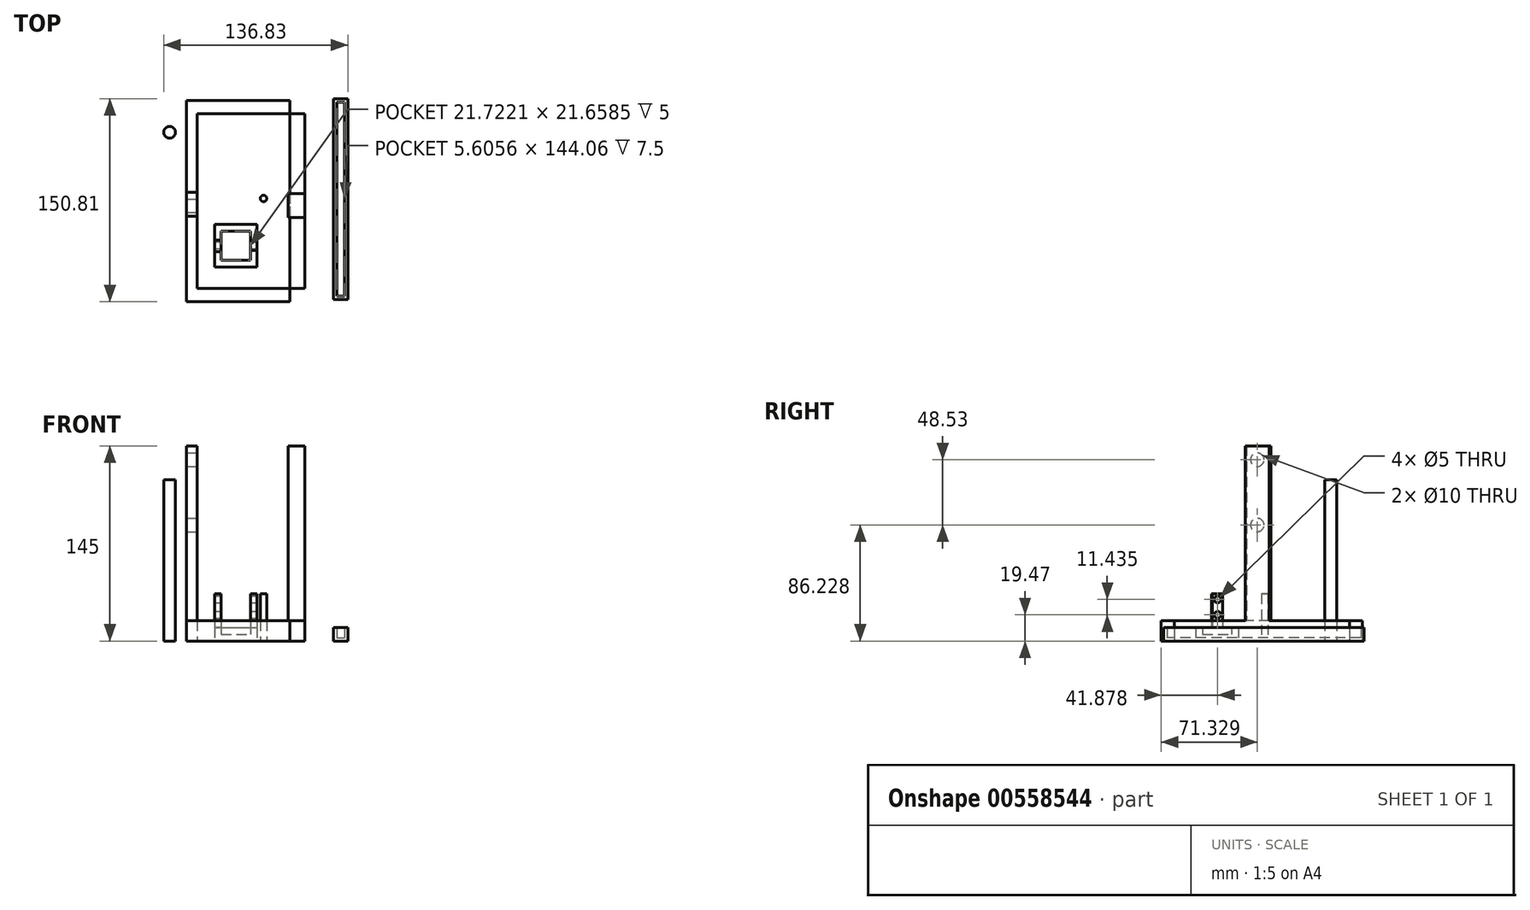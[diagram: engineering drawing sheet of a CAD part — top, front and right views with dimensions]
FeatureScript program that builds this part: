
annotation { "Feature Type Name" : "Feature", "Feature Type Description" : "" }
export const myFeature = defineFeature(function(context is Context, id is Id, definition is map)
    precondition{}
    {
        {
            var Q0;
            Q0=qCreatedBy(makeId("Top.planeOp"),FACE);
            var sketch = newSketch(context, id + "F0", { "sketchPlane" : qUnion([Q0])});
            skLineSegment(sketch, "E0.bottom", {"start": v(-51.22, 64.65) * mm, "end": v(47.83, 64.65) * mm});
            skLineSegment(sketch, "E0.top", {"start": v(-51.22, -66.38) * mm, "end": v(47.83, -66.38) * mm});
            skLineSegment(sketch, "E0.left", {"start": v(-51.22, 64.65) * mm, "end": v(-51.22, -66.38) * mm});
            skLineSegment(sketch, "E0.right", {"start": v(47.83, 64.65) * mm, "end": v(47.83, -66.38) * mm});
            skSolve(sketch);
        }
        {
            var Q0;
            Q0=makeQuery(id+"F0.imprint","IMPRINT",FACE,{"disambiguationData":[TD([[makeQuery(id+"F0.imprint","IMPRINT",EDGE,{"derivedFrom":sQuery(id+"F0.wireOp",EDGE,"E0.bottom")}),-1.0]])]});
            extrude(context, id + "F1", {"entities" : qUnion([Q0]), "depth" : 25 * mm, "offsetDistance" : 25 * mm});
        }
        {
            var Q0;
            Q0=makeQuery(id+"F1.opExtrude","CAP_FACE",FACE,{"disambiguationData":[OSD([sQuery(id+"F0.wireOp",EDGE,"E0.bottom"),sQuery(id+"F0.wireOp",EDGE,"E0.top"),sQuery(id+"F0.wireOp",EDGE,"E0.left"),sQuery(id+"F0.wireOp",EDGE,"E0.right")])],"isStart":false});
            var sketch = newSketch(context, id + "F2", { "sketchPlane" : qUnion([Q0])});
            skCircle(sketch, "E1", {"center": v(0, 1.77) * mm, "radius": 45.28 * mm});
            skSolve(sketch);
        }
        {
            var Q0;
            Q0=sQuery(id+"F2.wireOp",VERTEX,"E1.center");
            var Q1;
            Q1=makeQuery(id+"F1.opExtrude","SWEPT_BODY",BODY,{"disambiguationData":[OSD([sQuery(id+"F0.wireOp",EDGE,"E0.bottom"),sQuery(id+"F0.wireOp",EDGE,"E0.top"),sQuery(id+"F0.wireOp",EDGE,"E0.left"),sQuery(id+"F0.wireOp",EDGE,"E0.right")])]});
            hole(context, id + "F3", {"style" : HoleStyle.SIMPLE, "endStyle" : HoleEndStyle.THROUGH, "holeDiameter" : 80 * mm, "isTappedThrough" : true, "tappedDepth" : 12 * mm, "tapClearance" : 3, "locations" : qUnion([Q0]), "scope" : qUnion([Q1])});
        }
        {
            var Q0;
            Q0=makeQuery(id+"F1.opExtrude","CAP_FACE",FACE,{"disambiguationData":[OSD([sQuery(id+"F0.wireOp",EDGE,"E0.bottom"),sQuery(id+"F0.wireOp",EDGE,"E0.top"),sQuery(id+"F0.wireOp",EDGE,"E0.left"),sQuery(id+"F0.wireOp",EDGE,"E0.right")])],"isStart":false});
            var sketch = newSketch(context, id + "F4", { "sketchPlane" : qUnion([Q0])});
            skLineSegment(sketch, "E2.bottom", {"start": v(-51.22, 13.46) * mm, "end": v(-40.82, 13.46) * mm});
            skLineSegment(sketch, "E2.top", {"start": v(-51.22, -15.05) * mm, "end": v(-40.82, -15.05) * mm});
            skLineSegment(sketch, "E2.left", {"start": v(-51.22, 13.46) * mm, "end": v(-51.22, -15.05) * mm});
            skLineSegment(sketch, "E2.right", {"start": v(-40.82, 13.46) * mm, "end": v(-40.82, -15.05) * mm});
            skLineSegment(sketch, "E3.bottom", {"start": v(38.22, 13.56) * mm, "end": v(47.83, 13.56) * mm});
            skLineSegment(sketch, "E3.top", {"start": v(38.22, -17.64) * mm, "end": v(47.83, -17.64) * mm});
            skLineSegment(sketch, "E3.left", {"start": v(38.22, 13.56) * mm, "end": v(38.22, -17.64) * mm});
            skLineSegment(sketch, "E3.right", {"start": v(47.83, 13.56) * mm, "end": v(47.83, -17.64) * mm});
            skSolve(sketch);
        }
        {
            var Q0;
            Q0=makeQuery(id+"F4.imprint","IMPRINT",FACE,{"disambiguationData":[TD([[makeQuery(id+"F4.imprint","IMPRINT",EDGE,{"derivedFrom":sQuery(id+"F4.wireOp",EDGE,"E2.bottom")}),-1.0]])]});
            var Q1;
            {var subQ4=sQuery(id+"F4.wireOp",EDGE,"E3.bottom");Q1=makeQuery(id+"F4.imprint","IMPRINT",FACE,{"disambiguationData":[TD([[makeQuery(id+"F4.imprint","IMPRINT",EDGE,{"derivedFrom":subQ4}),-1.0]])]});}
            extrude(context, id + "F5", {"entities" : qUnion([Q0, Q1]), "operationType" : NewBodyOperationType.ADD, "depth" : 55 * mm, "offsetDistance" : 25 * mm});
        }
        {
            var Q0;
            Q0=makeQuery(id+"F5.boolean.opBoolean","MERGE",FACE,{"derivedFrom":[makeQuery(id+"F1.opExtrude","SWEPT_FACE",FACE,{"disambiguationData":[OSD([sQuery(id+"F0.wireOp",EDGE,"E0.left")])]}),makeQuery(id+"F5.opExtrude","SWEPT_FACE",FACE,{"disambiguationData":[OSD([sQuery(id+"F4.wireOp",EDGE,"E2.left")])]})]});
            var sketch = newSketch(context, id + "F6", { "sketchPlane" : qUnion([Q0])});
            skPoint(sketch, "E4", {"position": v(0, 69.65) * mm});
            skSolve(sketch);
        }
        {
            var Q0;
            Q0=sQuery(id+"F6.wireOp",VERTEX,"E4");
            var Q1;
            Q1=makeQuery(id+"F1.opExtrude","SWEPT_BODY",BODY,{"disambiguationData":[OSD([sQuery(id+"F0.wireOp",EDGE,"E0.bottom"),sQuery(id+"F0.wireOp",EDGE,"E0.top"),sQuery(id+"F0.wireOp",EDGE,"E0.left"),sQuery(id+"F0.wireOp",EDGE,"E0.right")])]});
            hole(context, id + "F7", {"style" : HoleStyle.SIMPLE, "endStyle" : HoleEndStyle.THROUGH, "holeDiameter" : 10 * mm, "isTappedThrough" : true, "tappedDepth" : 12 * mm, "tapClearance" : 3, "locations" : qUnion([Q0]), "scope" : qUnion([Q1])});
        }
        {
            var Q0;
            Q0=qCreatedBy(makeId("Top.planeOp"),FACE);
            var sketch = newSketch(context, id + "F8", { "sketchPlane" : qUnion([Q0])});
            skCircle(sketch, "E5", {"center": v(-69.75, 49.2) * mm, "radius": 4.39 * mm});
            skSolve(sketch);
        }
        {
            var Q0;
            Q0=makeQuery(id+"F8.imprint","IMPRINT",FACE,{"disambiguationData":[TD([[makeQuery(id+"F8.imprint","IMPRINT",EDGE,{"derivedFrom":sQuery(id+"F8.wireOp",EDGE,"E5")}),1.0]])]});
            extrude(context, id + "F9", {"entities" : qUnion([Q0]), "depth" : 120 * mm, "offsetDistance" : 25 * mm});
        }
        {
            var Q0;
            Q0=makeQuery(id+"F5.opExtrude","CAP_FACE",FACE,{"disambiguationData":[OSD([sQuery(id+"F4.wireOp",EDGE,"E2.bottom"),sQuery(id+"F4.wireOp",EDGE,"E2.top"),sQuery(id+"F4.wireOp",EDGE,"E2.left"),sQuery(id+"F4.wireOp",EDGE,"E2.right")])],"isStart":false});
            var Q1;
            Q1=makeQuery(id+"F5.opExtrude","CAP_FACE",FACE,{"disambiguationData":[OSD([sQuery(id+"F3.hole-0.sketch.wireOp",EDGE,"core_line_2"),sQuery(id+"F3.hole-0.sketch.wireOp",EDGE,"core_line_3"),sQuery(id+"F4.wireOp",EDGE,"E3.bottom"),sQuery(id+"F4.wireOp",EDGE,"E3.top"),sQuery(id+"F4.wireOp",EDGE,"E3.left"),sQuery(id+"F4.wireOp",EDGE,"E3.right")])],"isStart":false});
            extrude(context, id + "F10", {"entities" : qUnion([Q0, Q1]), "operationType" : NewBodyOperationType.ADD, "depth" : 60 * mm, "offsetDistance" : 25 * mm});
        }
        {
            var Q0;
            {var subQ0=sQuery(id+"F4.wireOp",EDGE,"E2.left");Q0=makeQuery(id+"F10.boolean.opBoolean","MERGE",FACE,{"derivedFrom":[makeQuery(id+"F5.boolean.opBoolean","MERGE",FACE,{"derivedFrom":[makeQuery(id+"F1.opExtrude","SWEPT_FACE",FACE,{"disambiguationData":[OSD([sQuery(id+"F0.wireOp",EDGE,"E0.left")])]}),makeQuery(id+"F5.opExtrude","SWEPT_FACE",FACE,{"disambiguationData":[OSD([subQ0])]})]}),makeQuery(id+"F10.opExtrude","SWEPT_FACE",FACE,{"disambiguationData":[OSD([subQ0])]})]});}
            var sketch = newSketch(context, id + "F11", { "sketchPlane" : qUnion([Q0])});
            skPoint(sketch, "E6", {"position": v(0, 129.87) * mm});
            skSolve(sketch);
        }
        {
            var Q0;
            Q0=sQuery(id+"F11.wireOp",VERTEX,"E6");
            var Q1;
            Q1=makeQuery(id+"F1.opExtrude","SWEPT_BODY",BODY,{"disambiguationData":[OSD([sQuery(id+"F0.wireOp",EDGE,"E0.bottom"),sQuery(id+"F0.wireOp",EDGE,"E0.top"),sQuery(id+"F0.wireOp",EDGE,"E0.left"),sQuery(id+"F0.wireOp",EDGE,"E0.right")])]});
            hole(context, id + "F12", {"style" : HoleStyle.SIMPLE, "endStyle" : HoleEndStyle.THROUGH, "holeDiameter" : 10 * mm, "isTappedThrough" : true, "tappedDepth" : 12 * mm, "tapClearance" : 3, "locations" : qUnion([Q0]), "scope" : qUnion([Q1])});
        }
        {
            var Q0;
            {var subQ0=sQuery(id+"F4.wireOp",EDGE,"E2.top");Q0=makeQuery(id+"F10.boolean.opBoolean","MERGE",FACE,{"derivedFrom":[makeQuery(id+"F5.opExtrude","SWEPT_FACE",FACE,{"disambiguationData":[OSD([subQ0])]}),makeQuery(id+"F10.opExtrude","SWEPT_FACE",FACE,{"disambiguationData":[OSD([subQ0])]})]});}
            extrude(context, id + "F13", {"entities" : qUnion([Q0]), "operationType" : NewBodyOperationType.ADD, "depth" : -5 * mm, "offsetDistance" : 25 * mm});
        }
        {
            var Q0;
            {var subQ0=sQuery(id+"F4.wireOp",EDGE,"E3.top");Q0=makeQuery(id+"F10.boolean.opBoolean","MERGE",FACE,{"derivedFrom":[makeQuery(id+"F5.opExtrude","SWEPT_FACE",FACE,{"disambiguationData":[OSD([subQ0])]}),makeQuery(id+"F10.opExtrude","SWEPT_FACE",FACE,{"disambiguationData":[OSD([subQ0])]})]});}
            extrude(context, id + "F14", {"entities" : qUnion([Q0]), "operationType" : NewBodyOperationType.ADD, "depth" : -5 * mm, "offsetDistance" : 25 * mm});
        }
        {
            var Q0;
            Q0=makeQuery(id+"F1.opExtrude","CAP_FACE",FACE,{"disambiguationData":[OSD([sQuery(id+"F0.wireOp",EDGE,"E0.bottom"),sQuery(id+"F0.wireOp",EDGE,"E0.top"),sQuery(id+"F0.wireOp",EDGE,"E0.left"),sQuery(id+"F0.wireOp",EDGE,"E0.right")])],"isStart":false});
            extrude(context, id + "F15", {"entities" : qUnion([Q0]), "operationType" : NewBodyOperationType.ADD, "depth" : -5 * mm, "offsetDistance" : 25 * mm});
        }
        {
            var Q0;
            Q0=makeQuery(id+"F1.opExtrude","CAP_FACE",FACE,{"disambiguationData":[OSD([sQuery(id+"F0.wireOp",EDGE,"E0.bottom"),sQuery(id+"F0.wireOp",EDGE,"E0.top"),sQuery(id+"F0.wireOp",EDGE,"E0.left"),sQuery(id+"F0.wireOp",EDGE,"E0.right")])],"isStart":false});
            extrude(context, id + "F16", {"entities" : qUnion([Q0]), "operationType" : NewBodyOperationType.ADD, "depth" : -10 * mm, "offsetDistance" : 25 * mm});
        }
        {
            var Q0;
            Q0=makeQuery(id+"F1.opExtrude","CAP_FACE",FACE,{"disambiguationData":[OSD([sQuery(id+"F0.wireOp",EDGE,"E0.bottom"),sQuery(id+"F0.wireOp",EDGE,"E0.top"),sQuery(id+"F0.wireOp",EDGE,"E0.left"),sQuery(id+"F0.wireOp",EDGE,"E0.right")])],"isStart":false});
            extrude(context, id + "F17", {"entities" : qUnion([Q0]), "operationType" : NewBodyOperationType.ADD, "depth" : -10 * mm, "offsetDistance" : 25 * mm});
        }
        {
            var Q0;
            Q0=qCreatedBy(makeId("Top.planeOp"),FACE);
            var sketch = newSketch(context, id + "F18", { "sketchPlane" : qUnion([Q0])});
            skLineSegment(sketch, "E7.bottom", {"start": v(52.09, 74.08) * mm, "end": v(62.7, 74.08) * mm});
            skLineSegment(sketch, "E7.top", {"start": v(52.09, -74.99) * mm, "end": v(62.7, -74.99) * mm});
            skLineSegment(sketch, "E7.left", {"start": v(52.09, 74.08) * mm, "end": v(52.09, -74.99) * mm});
            skLineSegment(sketch, "E7.right", {"start": v(62.7, 74.08) * mm, "end": v(62.7, -74.99) * mm});
            skSolve(sketch);
        }
        {
            var Q0;
            Q0=makeQuery(id+"F18.imprint","IMPRINT",FACE,{"disambiguationData":[TD([[makeQuery(id+"F18.imprint","IMPRINT",EDGE,{"derivedFrom":sQuery(id+"F18.wireOp",EDGE,"E7.bottom")}),-1.0]])]});
            extrude(context, id + "F19", {"entities" : qUnion([Q0]), "depth" : (10) * mm, "offsetDistance" : 25 * mm});
        }
        {
            var Q0;
            Q0=makeQuery(id+"F19.opExtrude","CAP_FACE",FACE,{"disambiguationData":[OSD([sQuery(id+"F18.wireOp",EDGE,"E7.bottom"),sQuery(id+"F18.wireOp",EDGE,"E7.top"),sQuery(id+"F18.wireOp",EDGE,"E7.left"),sQuery(id+"F18.wireOp",EDGE,"E7.right")])],"isStart":false});
            var Q1;
            Q1=makeQuery(id+"F1.opExtrude","CAP_FACE",FACE,{"disambiguationData":[OSD([sQuery(id+"F0.wireOp",EDGE,"E0.bottom"),sQuery(id+"F0.wireOp",EDGE,"E0.top"),sQuery(id+"F0.wireOp",EDGE,"E0.left"),sQuery(id+"F0.wireOp",EDGE,"E0.right")])],"isStart":false});
            shell(context, id + "F20", {"entities" : qUnion([Q0, Q1]), "thickness" : 2.5 * mm});
        }
        {
            var Q0;
            Q0=makeQuery(id+"F1.opExtrude","SWEPT_BODY",BODY,{"disambiguationData":[OSD([sQuery(id+"F0.wireOp",EDGE,"E0.bottom"),sQuery(id+"F0.wireOp",EDGE,"E0.top"),sQuery(id+"F0.wireOp",EDGE,"E0.left"),sQuery(id+"F0.wireOp",EDGE,"E0.right")])]});
            deleteBodies(context, id + "F21", {"entities" : qUnion([Q0])});
        }
        {
            var Q0;
            Q0=qCreatedBy(makeId("Top.planeOp"),FACE);
            var sketch = newSketch(context, id + "F22", { "sketchPlane" : qUnion([Q0])});
            skLineSegment(sketch, "E8.bottom", {"start": v(-57.26, -75.4) * mm, "end": v(-49.36, -75.4) * mm});
            skLineSegment(sketch, "E8.top", {"start": v(-57.26, 72.69) * mm, "end": v(-49.36, 72.69) * mm});
            skLineSegment(sketch, "E8.left", {"start": v(-57.26, -75.4) * mm, "end": v(-57.26, 72.69) * mm});
            skLineSegment(sketch, "E8.right", {"start": v(-49.36, -75.4) * mm, "end": v(-49.36, 72.69) * mm});
            skLineSegment(sketch, "E9.bottom", {"start": v(-57.26, 72.69) * mm, "end": v(30.72, 72.69) * mm});
            skLineSegment(sketch, "E9.top", {"start": v(-57.26, 63.12) * mm, "end": v(30.72, 63.12) * mm});
            skLineSegment(sketch, "E9.left", {"start": v(-57.26, 72.69) * mm, "end": v(-57.26, 63.12) * mm});
            skLineSegment(sketch, "E9.right", {"start": v(30.72, 72.69) * mm, "end": v(30.72, 63.12) * mm});
            skLineSegment(sketch, "E10.bottom", {"start": v(30.72, 72.69) * mm, "end": v(19.72, 72.69) * mm});
            skLineSegment(sketch, "E10.top", {"start": v(30.72, -76.73) * mm, "end": v(19.72, -76.73) * mm});
            skLineSegment(sketch, "E10.left", {"start": v(30.72, 72.69) * mm, "end": v(30.72, -76.73) * mm});
            skLineSegment(sketch, "E10.right", {"start": v(19.72, 72.69) * mm, "end": v(19.72, -76.73) * mm});
            skLineSegment(sketch, "E11.bottom", {"start": v(30.72, -76.73) * mm, "end": v(-57.26, -76.73) * mm});
            skLineSegment(sketch, "E11.top", {"start": v(30.72, -66.94) * mm, "end": v(-57.26, -66.94) * mm});
            skLineSegment(sketch, "E11.left", {"start": v(30.72, -76.73) * mm, "end": v(30.72, -66.94) * mm});
            skLineSegment(sketch, "E11.right", {"start": v(-57.26, -76.73) * mm, "end": v(-57.26, -66.94) * mm});
            skSolve(sketch);
        }
        {
            var Q0;
            {var subQ8=sQuery(id+"F22.wireOp",EDGE,"E8.bottom");Q0=makeQuery(id+"F22.imprint","IMPRINT",FACE,{"disambiguationData":[TD([[makeQuery(id+"F22.imprint","IMPRINT",EDGE,{"derivedFrom":subQ8}),-1.0]])]});}
            var Q1;
            {var subQ0=sQuery(id+"F22.wireOp",EDGE,"E8.bottom");Q1=makeQuery(id+"F22.imprint","IMPRINT",FACE,{"disambiguationData":[TD([[makeQuery(id+"F22.imprint","IMPRINT",EDGE,{"derivedFrom":subQ0}),1.0]])]});}
            var Q2;
            {var subQ0=sQuery(id+"F22.wireOp",EDGE,"E8.left");Q2=makeQuery(id+"F22.imprint","IMPRINT",FACE,{"disambiguationData":[TD([[makeQuery(id+"F22.imprint","IMPRINT",EDGE,{"derivedFrom":subQ0}),-1.0]])]});}
            var Q3;
            {var subQ5=sQuery(id+"F22.wireOp",EDGE,"E9.left");Q3=makeQuery(id+"F22.imprint","IMPRINT",FACE,{"disambiguationData":[TD([[makeQuery(id+"F22.imprint","IMPRINT",EDGE,{"derivedFrom":subQ5}),1.0]])]});}
            var Q4;
            {var subQ0=sQuery(id+"F22.wireOp",EDGE,"E9.bottom");var subQ1=sQuery(id+"F22.wireOp",EDGE,"E8.right");var subQ2=makeQuery(id+"F22.imprint","INTERSECT",VERTEX,{"derivedFrom":[subQ1,subQ0]});Q4=makeQuery(id+"F22.imprint","IMPRINT",FACE,{"disambiguationData":[TD([[makeQuery(id+"F22.imprint","IMPRINT",EDGE,{"disambiguationData":[TD([[subQ2,1.0]])],"derivedFrom":subQ1}),-1.0]])]});}
            var Q5;
            {var subQ5=sQuery(id+"F22.wireOp",EDGE,"E10.bottom");Q5=makeQuery(id+"F22.imprint","IMPRINT",FACE,{"disambiguationData":[TD([[makeQuery(id+"F22.imprint","IMPRINT",EDGE,{"derivedFrom":subQ5}),1.0]])]});}
            var Q6;
            {var subQ0=sQuery(id+"F22.wireOp",EDGE,"E10.left");var subQ1=sQuery(id+"F22.wireOp",EDGE,"E9.top");var subQ2=makeQuery(id+"F22.imprint","INTERSECT",VERTEX,{"derivedFrom":[subQ1,subQ0]});Q6=makeQuery(id+"F22.imprint","IMPRINT",FACE,{"disambiguationData":[TD([[makeQuery(id+"F22.imprint","IMPRINT",EDGE,{"disambiguationData":[TD([[subQ2,1.0]])],"derivedFrom":subQ1}),-1.0]])]});}
            var Q7;
            {var subQ5=sQuery(id+"F22.wireOp",EDGE,"E11.left");Q7=makeQuery(id+"F22.imprint","IMPRINT",FACE,{"disambiguationData":[TD([[makeQuery(id+"F22.imprint","IMPRINT",EDGE,{"derivedFrom":subQ5}),1.0]])]});}
            extrude(context, id + "F23", {"entities" : qUnion([Q0, Q1, Q2, Q3, Q4, Q5, Q6, Q7]), "depth" : 15 * mm, "offsetDistance" : 25 * mm});
        }
        {
            var Q0;
            Q0=makeQuery(id+"F23.opExtrude","CAP_FACE",FACE,{"disambiguationData":[OSD([sQuery(id+"F22.wireOp",EDGE,"E8.left"),sQuery(id+"F22.wireOp",EDGE,"E8.right"),sQuery(id+"F22.wireOp",EDGE,"E9.bottom"),sQuery(id+"F22.wireOp",EDGE,"E9.top"),sQuery(id+"F22.wireOp",EDGE,"E9.left"),sQuery(id+"F22.wireOp",EDGE,"E10.bottom"),sQuery(id+"F22.wireOp",EDGE,"E10.left"),sQuery(id+"F22.wireOp",EDGE,"E10.right"),sQuery(id+"F22.wireOp",EDGE,"E11.bottom"),sQuery(id+"F22.wireOp",EDGE,"E11.top"),sQuery(id+"F22.wireOp",EDGE,"E11.left"),sQuery(id+"F22.wireOp",EDGE,"E11.right")])],"isStart":false});
            var sketch = newSketch(context, id + "F24", { "sketchPlane" : qUnion([Q0])});
            skLineSegment(sketch, "E12.bottom", {"start": v(-57.26, -13.27) * mm, "end": v(-49.36, -13.27) * mm});
            skLineSegment(sketch, "E12.top", {"start": v(-57.26, 4.71) * mm, "end": v(-49.36, 4.71) * mm});
            skLineSegment(sketch, "E12.left", {"start": v(-57.26, -13.27) * mm, "end": v(-57.26, 4.71) * mm});
            skLineSegment(sketch, "E12.right", {"start": v(-49.36, -13.27) * mm, "end": v(-49.36, 4.71) * mm});
            skPoint(sketch, "E13", {"position": v(-49.36, -13.27) * mm});
            skLineSegment(sketch, "E14.bottom", {"start": v(30.72, 3.46) * mm, "end": v(18.19, 3.46) * mm});
            skLineSegment(sketch, "E14.top", {"start": v(30.72, -14.26) * mm, "end": v(18.19, -14.26) * mm});
            skLineSegment(sketch, "E14.left", {"start": v(30.72, 3.46) * mm, "end": v(30.72, -14.26) * mm});
            skLineSegment(sketch, "E14.right", {"start": v(18.19, 3.46) * mm, "end": v(18.19, -14.26) * mm});
            skPoint(sketch, "E14.middle", {"position": v(24.45, -5.4) * mm});
            skSolve(sketch);
        }
        {
            var Q0;
            Q0=makeQuery(id+"F24.imprint","IMPRINT",FACE,{"disambiguationData":[TD([[makeQuery(id+"F24.imprint","IMPRINT",EDGE,{"derivedFrom":sQuery(id+"F24.wireOp",EDGE,"E12.bottom")}),1.0]])]});
            var Q1;
            {var subQ0=sQuery(id+"F24.wireOp",EDGE,"E14.left");Q1=makeQuery(id+"F24.imprint","IMPRINT",FACE,{"disambiguationData":[TD([[makeQuery(id+"F24.imprint","IMPRINT",EDGE,{"derivedFrom":subQ0}),-1.0]])]});}
            extrude(context, id + "F25", {"entities" : qUnion([Q0, Q1]), "operationType" : NewBodyOperationType.ADD, "depth" : 130 * mm, "offsetDistance" : 25 * mm});
        }
        {
            var Q0;
            Q0=makeQuery(id+"F25.boolean.opBoolean","MERGE",FACE,{"derivedFrom":[makeQuery(id+"F23.opExtrude","SWEPT_FACE",FACE,{"disambiguationData":[OSD([sQuery(id+"F22.wireOp",EDGE,"E10.left"),sQuery(id+"F22.wireOp",EDGE,"E11.left")])]}),makeQuery(id+"F25.opExtrude","SWEPT_FACE",FACE,{"disambiguationData":[OSD([sQuery(id+"F24.wireOp",EDGE,"E14.left")])]})]});
            var sketch = newSketch(context, id + "F26", { "sketchPlane" : qUnion([Q0])});
            skPoint(sketch, "E15", {"position": v(-5.4, 134.76) * mm});
            skPoint(sketch, "E15.positionSnap0", {"position": v(-5.4, 145) * mm});
            skPoint(sketch, "E16", {"position": v(-5.4, 86.23) * mm});
            skSolve(sketch);
        }
        {
            var Q0;
            Q0=sQuery(id+"F26.wireOp",VERTEX,"E15");
            var Q1;
            Q1=sQuery(id+"F26.wireOp",VERTEX,"E16");
            var Q2;
            Q2=makeQuery(id+"F23.opExtrude","SWEPT_BODY",BODY,{"disambiguationData":[OSD([sQuery(id+"F22.wireOp",EDGE,"E8.left"),sQuery(id+"F22.wireOp",EDGE,"E8.right"),sQuery(id+"F22.wireOp",EDGE,"E9.bottom"),sQuery(id+"F22.wireOp",EDGE,"E9.top"),sQuery(id+"F22.wireOp",EDGE,"E9.left"),sQuery(id+"F22.wireOp",EDGE,"E10.bottom"),sQuery(id+"F22.wireOp",EDGE,"E10.left"),sQuery(id+"F22.wireOp",EDGE,"E10.right"),sQuery(id+"F22.wireOp",EDGE,"E11.bottom"),sQuery(id+"F22.wireOp",EDGE,"E11.top"),sQuery(id+"F22.wireOp",EDGE,"E11.left"),sQuery(id+"F22.wireOp",EDGE,"E11.right")])]});
            hole(context, id + "F27", {"style" : HoleStyle.SIMPLE, "endStyle" : HoleEndStyle.THROUGH, "holeDiameter" : 10 * mm, "isTappedThrough" : true, "tappedDepth" : 12 * mm, "tapClearance" : 3, "locations" : qUnion([Q0, Q1]), "scope" : qUnion([Q2])});
        }
        {
            var Q0;
            Q0=qCreatedBy(makeId("Top.planeOp"),FACE);
            var sketch = newSketch(context, id + "F28", { "sketchPlane" : qUnion([Q0])});
            skLineSegment(sketch, "E17.bottom", {"start": v(-36.45, -51) * mm, "end": v(-4.73, -51) * mm});
            skLineSegment(sketch, "E17.top", {"start": v(-36.45, -19.34) * mm, "end": v(-4.73, -19.34) * mm});
            skLineSegment(sketch, "E17.left", {"start": v(-36.45, -51) * mm, "end": v(-36.45, -19.34) * mm});
            skLineSegment(sketch, "E17.right", {"start": v(-4.73, -51) * mm, "end": v(-4.73, -19.34) * mm});
            skSolve(sketch);
        }
        {
            var Q0;
            Q0=makeQuery(id+"F28.imprint","IMPRINT",FACE,{"disambiguationData":[TD([[makeQuery(id+"F28.imprint","IMPRINT",EDGE,{"derivedFrom":sQuery(id+"F28.wireOp",EDGE,"E17.bottom")}),1.0]])]});
            extrude(context, id + "F29", {"entities" : qUnion([Q0]), "depth" : 5 * mm, "offsetDistance" : 25 * mm});
        }
        {
            var Q0;
            Q0=makeQuery(id+"F29.opExtrude","CAP_FACE",FACE,{"disambiguationData":[OSD([sQuery(id+"F28.wireOp",EDGE,"E17.bottom"),sQuery(id+"F28.wireOp",EDGE,"E17.top"),sQuery(id+"F28.wireOp",EDGE,"E17.left"),sQuery(id+"F28.wireOp",EDGE,"E17.right")])],"isStart":false});
            extrude(context, id + "F30", {"entities" : qUnion([Q0]), "operationType" : NewBodyOperationType.ADD, "depth" : 5 * mm, "offsetDistance" : 25 * mm});
        }
        {
            var Q0;
            Q0=makeQuery(id+"F30.opExtrude","CAP_FACE",FACE,{"disambiguationData":[OSD([sQuery(id+"F28.wireOp",EDGE,"E17.bottom"),sQuery(id+"F28.wireOp",EDGE,"E17.top"),sQuery(id+"F28.wireOp",EDGE,"E17.left"),sQuery(id+"F28.wireOp",EDGE,"E17.right")])],"isStart":false});
            shell(context, id + "F31", {"entities" : qUnion([Q0]), "thickness" : 5 * mm});
        }
        {
            var Q0;
            Q0=makeQuery(id+"F30.opExtrude","CAP_FACE",FACE,{"disambiguationData":[OSD([sQuery(id+"F28.wireOp",EDGE,"E17.bottom"),sQuery(id+"F28.wireOp",EDGE,"E17.top"),sQuery(id+"F28.wireOp",EDGE,"E17.left"),sQuery(id+"F28.wireOp",EDGE,"E17.right")])],"isStart":false});
            var sketch = newSketch(context, id + "F32", { "sketchPlane" : qUnion([Q0])});
            skLineSegment(sketch, "E18.bottom", {"start": v(-31.45, -39.46) * mm, "end": v(-36.45, -39.46) * mm});
            skLineSegment(sketch, "E18.top", {"start": v(-31.45, -31.13) * mm, "end": v(-36.45, -31.13) * mm});
            skLineSegment(sketch, "E18.left", {"start": v(-31.45, -39.46) * mm, "end": v(-31.45, -31.13) * mm});
            skLineSegment(sketch, "E18.right", {"start": v(-36.45, -39.46) * mm, "end": v(-36.45, -31.13) * mm});
            skLineSegment(sketch, "E19.bottom", {"start": v(-9.73, -38.68) * mm, "end": v(-4.73, -38.68) * mm});
            skLineSegment(sketch, "E19.top", {"start": v(-9.73, -31.13) * mm, "end": v(-4.73, -31.13) * mm});
            skLineSegment(sketch, "E19.left", {"start": v(-9.73, -38.68) * mm, "end": v(-9.73, -31.13) * mm});
            skLineSegment(sketch, "E19.right", {"start": v(-4.73, -38.68) * mm, "end": v(-4.73, -31.13) * mm});
            skSolve(sketch);
        }
        {
            var Q0;
            Q0=makeQuery(id+"F32.imprint","IMPRINT",FACE,{"disambiguationData":[TD([[makeQuery(id+"F32.imprint","IMPRINT",EDGE,{"derivedFrom":sQuery(id+"F32.wireOp",EDGE,"E18.bottom")}),-1.0]])]});
            var Q1;
            Q1=makeQuery(id+"F32.imprint","IMPRINT",FACE,{"disambiguationData":[TD([[makeQuery(id+"F32.imprint","IMPRINT",EDGE,{"derivedFrom":sQuery(id+"F32.wireOp",EDGE,"E19.bottom")}),1.0]])]});
            extrude(context, id + "F33", {"entities" : qUnion([Q0, Q1]), "operationType" : NewBodyOperationType.ADD, "depth" : 25 * mm, "offsetDistance" : 25 * mm});
        }
        {
            var Q0;
            {var subQ0=sQuery(id+"F28.wireOp",EDGE,"E17.right");Q0=makeQuery(id+"F33.boolean.opBoolean","MERGE",FACE,{"derivedFrom":[makeQuery(id+"F30.boolean.opBoolean","MERGE",FACE,{"derivedFrom":[makeQuery(id+"F29.opExtrude","SWEPT_FACE",FACE,{"disambiguationData":[OSD([subQ0])]}),makeQuery(id+"F30.opExtrude","SWEPT_FACE",FACE,{"disambiguationData":[OSD([subQ0])]})]}),makeQuery(id+"F33.opExtrude","SWEPT_FACE",FACE,{"disambiguationData":[OSD([sQuery(id+"F32.wireOp",EDGE,"E19.right")])]})]});}
            var sketch = newSketch(context, id + "F34", { "sketchPlane" : qUnion([Q0])});
            skPoint(sketch, "E20", {"position": v(-34.85, 30.9) * mm});
            skPoint(sketch, "E21", {"position": v(-34.85, 19.47) * mm});
            skSolve(sketch);
        }
        {
            var Q0;
            Q0=sQuery(id+"F34.wireOp",VERTEX,"E20");
            var Q1;
            Q1=sQuery(id+"F34.wireOp",VERTEX,"E21");
            var Q2;
            Q2=makeQuery(id+"F29.opExtrude","SWEPT_BODY",BODY,{"disambiguationData":[OSD([sQuery(id+"F28.wireOp",EDGE,"E17.bottom"),sQuery(id+"F28.wireOp",EDGE,"E17.top"),sQuery(id+"F28.wireOp",EDGE,"E17.left"),sQuery(id+"F28.wireOp",EDGE,"E17.right")])]});
            hole(context, id + "F35", {"style" : HoleStyle.SIMPLE, "endStyle" : HoleEndStyle.THROUGH, "holeDiameter" : 5 * mm, "isTappedThrough" : true, "tappedDepth" : 12 * mm, "tapClearance" : 3, "locations" : qUnion([Q0, Q1]), "scope" : qUnion([Q2])});
        }
        {
            var Q0;
            Q0=qCreatedBy(makeId("Top.planeOp"),FACE);
            var sketch = newSketch(context, id + "F36", { "sketchPlane" : qUnion([Q0])});
            skCircle(sketch, "E22", {"center": v(0, 0) * mm, "radius": 2.38 * mm});
            skSolve(sketch);
        }
        {
            var Q0;
            Q0=makeQuery(id+"F36.imprint","IMPRINT",FACE,{"disambiguationData":[TD([[makeQuery(id+"F36.imprint","IMPRINT",EDGE,{"derivedFrom":sQuery(id+"F36.wireOp",EDGE,"E22")}),1.0]])]});
            extrude(context, id + "F37", {"entities" : qUnion([Q0]), "depth" : 35 * mm, "offsetDistance" : 25 * mm});
        }
    });
